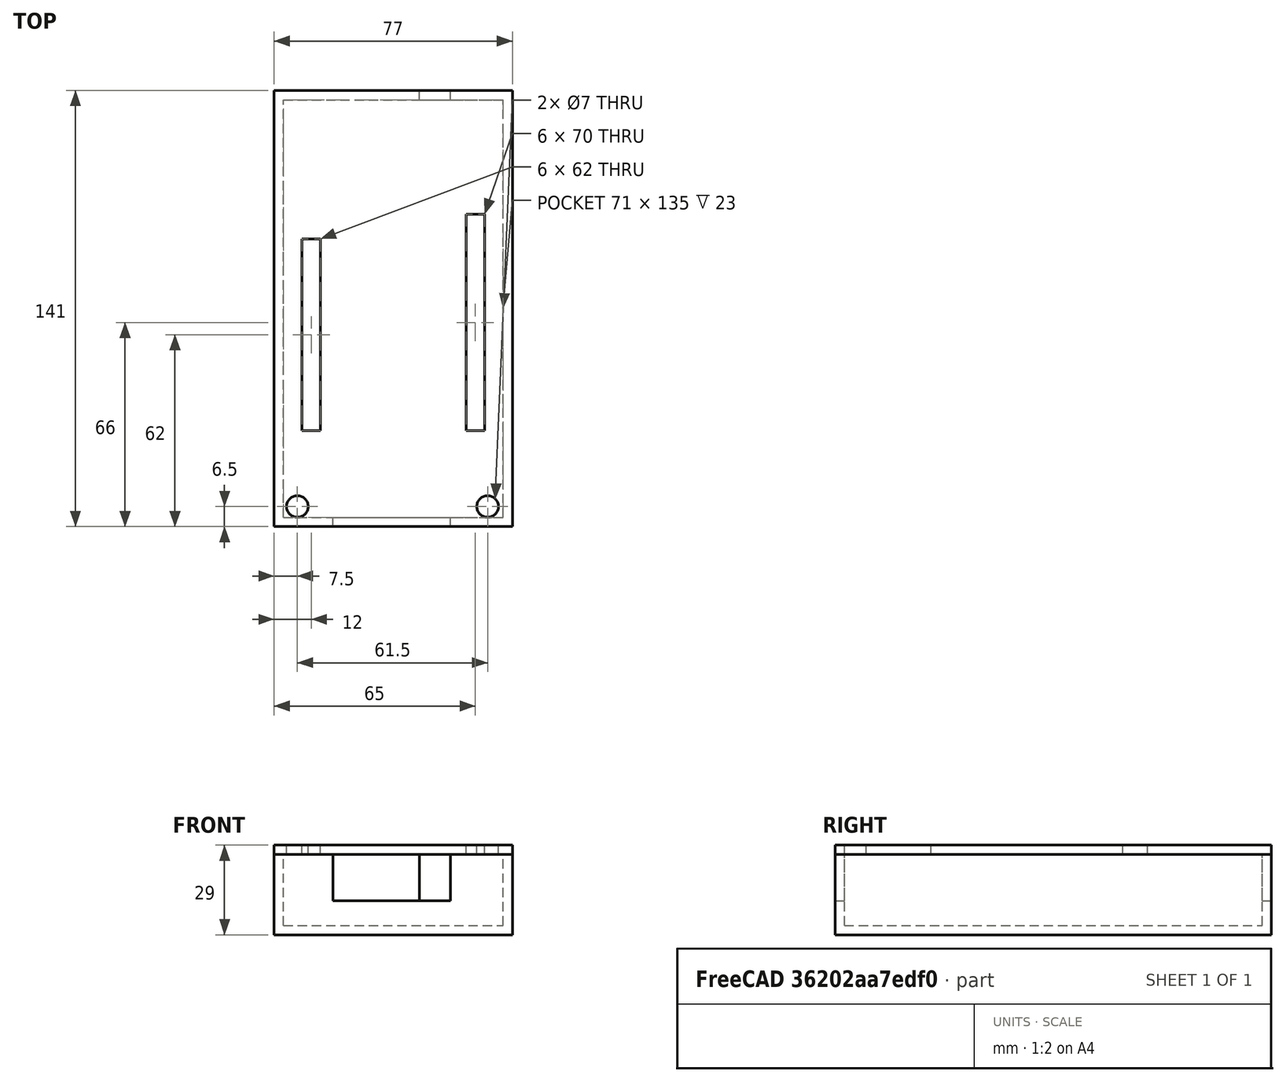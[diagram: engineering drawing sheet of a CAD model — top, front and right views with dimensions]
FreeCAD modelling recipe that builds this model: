
FCSTD DOCUMENT  (FreeCAD 0.16R6706 (Git))
Label: F767ZI
License: All rights reserved
LicenseURL: http://en.wikipedia.org/wiki/All_rights_reserved
objects: Part::Box×8, Part::Cut×5, Part::MultiFuse×3, Part::Cylinder×2
note: 18 computed .brp shape members not serialized (recipe doc carries the construction recipe); baked Part::Feature solids carry a one-line shape summary decoded from their .brp

FEATURE [Part::Box] Box  label="a"
  Height = 23
  Length = 77
  Width = 141
FEATURE [Part::Box] Box001  label="b"
  Height = 23
  Length = 71
  Placement = pos=(3,3,0) rot=(0,0,1;0rad)
  Width = 135
FEATURE [Part::Cut] Cut  label="1"
  Base = -> Box
  Placement = pos=(0,0,3) rot=(0,0,1;0rad)
  Tool = -> Box001
FEATURE [Part::Box] Box002  label="2"
  Height = 3
  Length = 77
  Width = 141
FEATURE [Part::MultiFuse] Fusion  label="3"
  Shapes = -> [Cut,Box002]
FEATURE [Part::Box] Box003  label="4"
  Height = 15
  Length = 38
  Placement = pos=(19,0,11) rot=(0,0,1;0rad)
  Width = 3
FEATURE [Part::Cut] Cut001  label="carcasa_B"
  Base = -> Fusion
  Tool = -> Box003
FEATURE [Part::Box] Box004  label="5"
  Height = 15
  Length = 10
  Placement = pos=(47,138,11) rot=(0,0,1;0rad)
  Width = 3
FEATURE [Part::Cut] Cut002  label="carcasa"
  Base = -> Cut001
  Tool = -> Box004
FEATURE [Part::Box] Box005  label="01"
  Height = 3
  Length = 77
  Placement = pos=(0,0,26) rot=(0,0,1;0rad)
  Width = 141
FEATURE [Part::Cylinder] Cylinder  label="switch1"
  Angle = 360
  Height = 3
  Placement = pos=(7.5,5.5,26) rot=(0,0,1;0rad)
  Radius = 3.5
FEATURE [Part::Cylinder] Cylinder001  label="switch2"
  Angle = 360
  Height = 3
  Placement = pos=(69,5.5,26) rot=(0,0,1;0rad)
  Radius = 3.5
FEATURE [Part::MultiFuse] Fusion001  label="switches"
  Placement = pos=(0,1,0) rot=(0,0,1;0rad)
  Shapes = -> [Cylinder,Cylinder001]
FEATURE [Part::Cut] Cut003  label="02"
  Base = -> Box005
  Tool = -> Fusion001
FEATURE [Part::Box] Box006  label="rejilla1"
  Height = 3
  Length = 6
  Placement = pos=(9,31,26) rot=(0,0,1;0rad)
  Width = 62
FEATURE [Part::Box] Box007  label="rejilla2"
  Height = 3
  Length = 6
  Placement = pos=(62,31,26) rot=(0,0,1;0rad)
  Width = 70
FEATURE [Part::MultiFuse] Fusion002  label="rejillas"
  Shapes = -> [Box006,Box007]
FEATURE [Part::Cut] Cut004  label="tapa"
  Base = -> Cut003
  Tool = -> Fusion002
